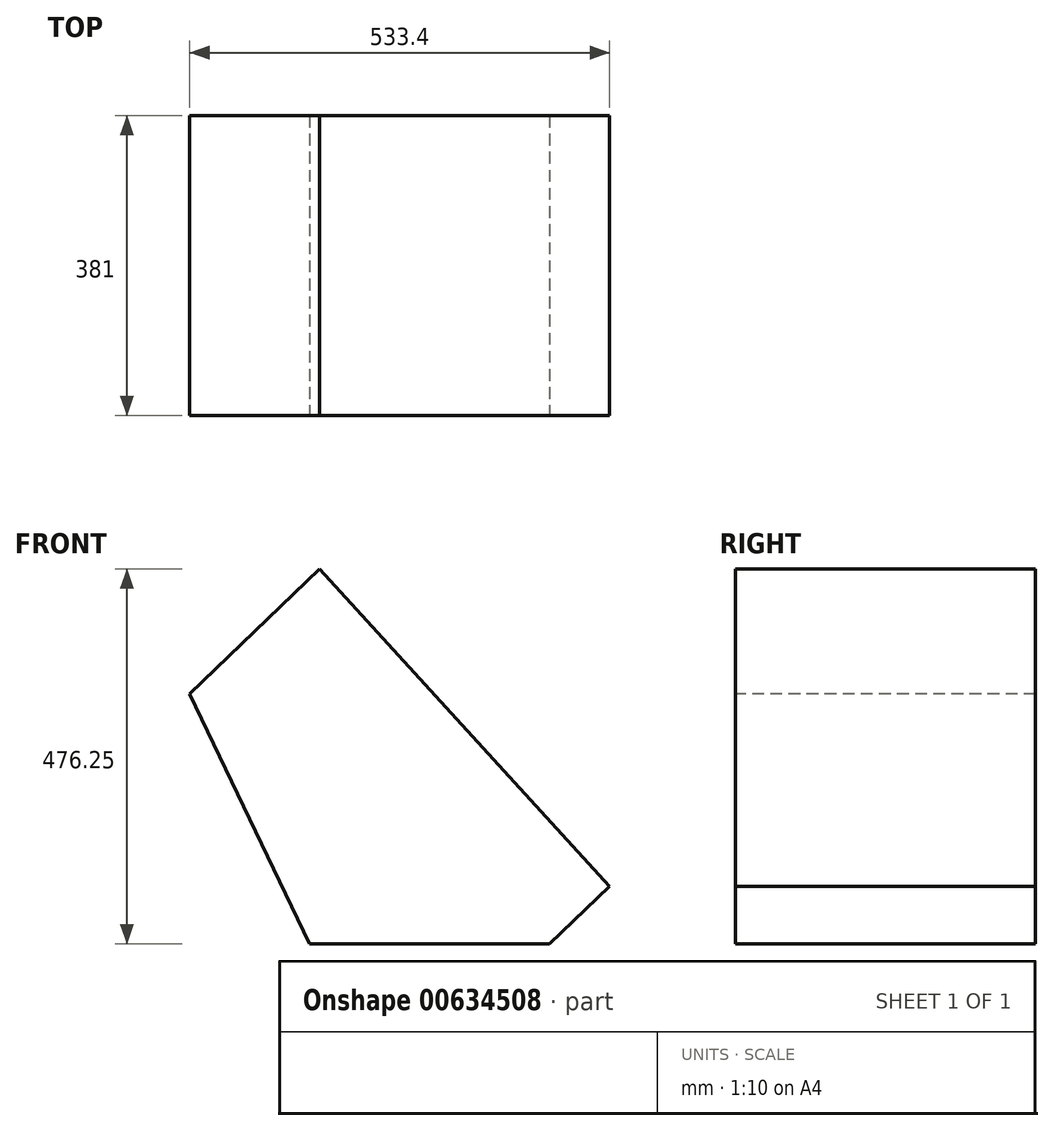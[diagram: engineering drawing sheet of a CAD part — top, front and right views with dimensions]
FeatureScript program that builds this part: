
annotation { "Feature Type Name" : "Feature", "Feature Type Description" : "" }
export const myFeature = defineFeature(function(context is Context, id is Id, definition is map)
    precondition{}
    {
        {
            var Q0;
            Q0=qCreatedBy(makeId("Front.planeOp"),FACE);
            var sketch = newSketch(context, id + "F0", { "sketchPlane" : qUnion([Q0])});
            skLineSegment(sketch, "E0", {"start": v(0, 317.82) * mm, "end": v(152.4, 0) * mm});
            skLineSegment(sketch, "E1", {"start": v(152.4, 0) * mm, "end": v(457.2, 0) * mm});
            skLineSegment(sketch, "E2", {"start": v(457.2, 0) * mm, "end": v(533.4, 73.26) * mm});
            skLineSegment(sketch, "E3", {"start": v(533.4, 73.26) * mm, "end": v(164.8, 476.25) * mm});
            skLineSegment(sketch, "E4", {"start": v(164.8, 476.25) * mm, "end": v(0, 317.82) * mm});
            skSolve(sketch);
        }
        {
            var Q0;
            Q0=makeQuery(id+"F0.imprint","IMPRINT",FACE,{"disambiguationData":[TD([[makeQuery(id+"F0.imprint","IMPRINT",EDGE,{"derivedFrom":sQuery(id+"F0.wireOp",EDGE,"E0")}),1.0]])]});
            extrude(context, id + "F1", {"entities" : qUnion([Q0]), "oppositeDirection" : true, "depth" : 381 * mm});
        }
    });
